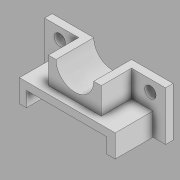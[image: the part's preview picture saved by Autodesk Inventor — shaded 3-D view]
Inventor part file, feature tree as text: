
AUTODESK INVENTOR PART (.ipt)
format: ipt  version: 2020 (Build 240168000, 168)  size: 151,552 bytes
history: native  units: in
note: dims shown in document units (in); Inventor stores cm internally (conversion verified against a paired STEP export)
features: extrude x7, sketch x7, other x1
ambient origin geometry x8: Origin, YZ Plane, XZ Plane, XY Plane, X Axis, Y Axis, Z Axis, Center Point
bodies: Body1 (feature_tree)
feature tree (15):
  other  "Sólido1"
  extrude  "Extrusión1"  Depth=2.4375in
  extrude  "Extrusión2"  Depth=4.75in
  extrude  "Extrusión3"  Depth=1.125in
  extrude  "Extrusión4"  Depth=2.625in
  extrude  "Extrusión5"  Depth=1.3125in
  extrude  "Extrusión6"  Depth=4.0in
  extrude  "Extrusión7"  Depth=1.875in TaperAngle=0.0deg
  sketch  "Boceto1"  dims[d0=6.0in d1=2.4375in]
  sketch  "Boceto2"  dims[d2=0.375in d3=0.0in d4=4.75in]
  sketch  "Boceto3"  dims[d5=1.125in d6=2.375in]
  sketch  "Boceto4"  dims[d7=1.875in d8=0.0in d9=2.625in]
  sketch  "Boceto5"  dims[d10=1.3125in d11=1.3125in]
  sketch  "Boceto6"  dims[d12=1.5in d13=0.0in d14=4.0in]
  sketch  "Boceto7"  dims[d15=0.75in d16=1.875in d17=0.0in d18=0.938in d19=0.0in d20=1.875in d21=1.875in d22=0.0in d23=0.5625in d24=0.75in d25=0.5625in d26=0.375in d27=0.0in d28=0.75in d29=0.5625in d30=0.5625in d31=0.375in d32=0.0in]
